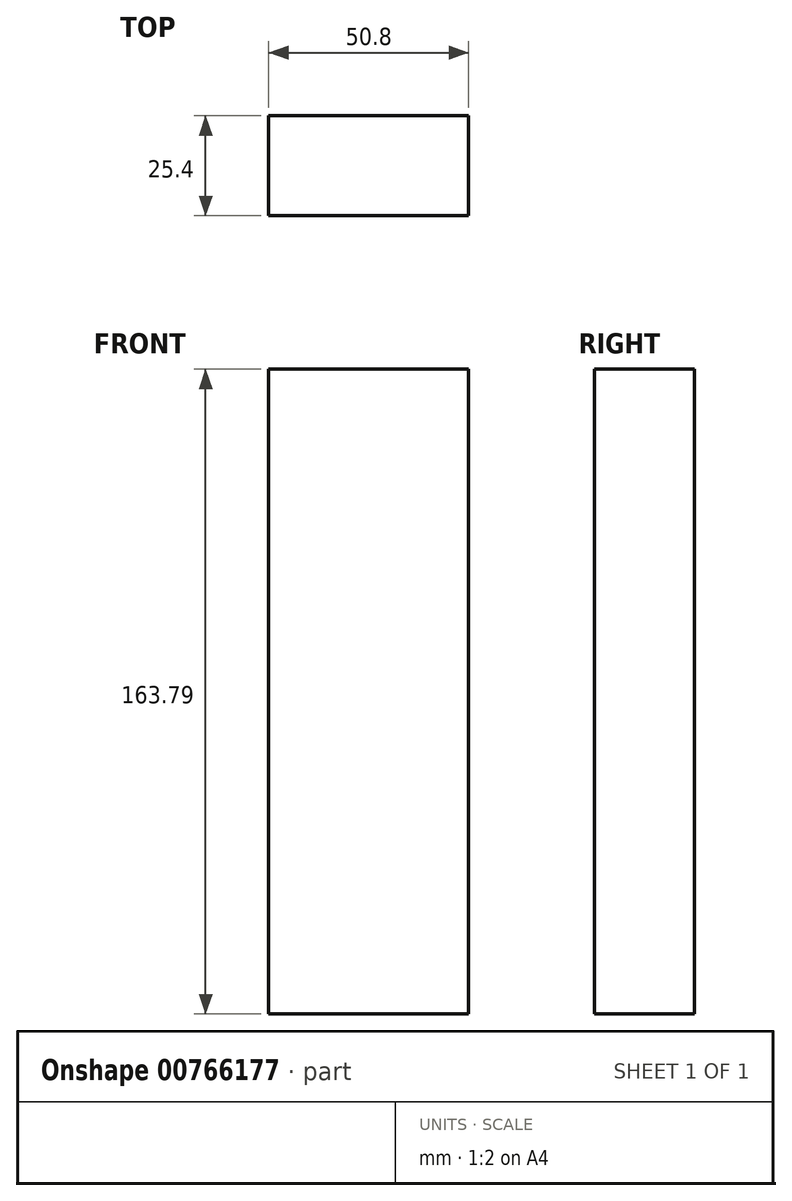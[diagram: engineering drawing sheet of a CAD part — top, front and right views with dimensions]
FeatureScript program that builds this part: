
annotation { "Feature Type Name" : "Feature", "Feature Type Description" : "" }
export const myFeature = defineFeature(function(context is Context, id is Id, definition is map)
    precondition{}
    {
        {
            var Q0;
            Q0=qCreatedBy(makeId("Front.planeOp"),FACE);
            var sketch = newSketch(context, id + "F0", { "sketchPlane" : qUnion([Q0])});
            skLineSegment(sketch, "E0.bottom", {"start": v(-43.3, 65.38) * mm, "end": v(7.5, 65.38) * mm});
            skLineSegment(sketch, "E0.top", {"start": v(-43.3, -98.41) * mm, "end": v(7.5, -98.41) * mm});
            skLineSegment(sketch, "E0.left", {"start": v(-43.3, 65.38) * mm, "end": v(-43.3, -98.41) * mm});
            skLineSegment(sketch, "E0.right", {"start": v(7.5, 65.38) * mm, "end": v(7.5, -98.41) * mm});
            skSolve(sketch);
        }
        {
            var Q0;
            Q0=makeQuery(id+"F0.imprint","IMPRINT",FACE,{"disambiguationData":[TD([[makeQuery(id+"F0.imprint","IMPRINT",EDGE,{"derivedFrom":sQuery(id+"F0.wireOp",EDGE,"E0.bottom")}),-1.0]])]});
            extrude(context, id + "F1", {"entities" : qUnion([Q0]), "depth" : 25.4 * mm, "offsetDistance" : 25.4 * mm});
        }
    });
